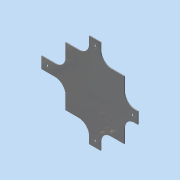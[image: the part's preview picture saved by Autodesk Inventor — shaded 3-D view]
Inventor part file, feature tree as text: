
AUTODESK INVENTOR PART (.ipt)
format: ipt  version: 2015 (Build 190159000, 159)  size: 314,880 bytes
history: native  units: in
note: dims shown in document units (in); Inventor stores cm internally (conversion verified against a paired STEP export)
features: sketch x21, projected_geometry x16, extrude x11, hole x10, pattern_circular x4, chamfer x2, plane x2
ambient origin geometry x8: Origin, YZ Plane, XZ Plane, XY Plane, X Axis, Y Axis, Z Axis, Center Point
bodies: Solid1 (feature_tree)
feature tree (66):
  extrude  "Extrusion1"  Depth=11.811in
  hole  "Hole1"  [1 undecoded]
  hole  "Hole2"  [1 undecoded]
  hole  "Hole3"  [1 undecoded]
  chamfer  "Chamfer1"  Distance=0.125in Angle=45.0deg
  chamfer  "Chamfer2"  Distance=0.125in Angle=45.0deg
  sketch  "Sketch5"  dims[d9=0.2756in]
  extrude  "Extrusion2"  Depth=5.9055in
  plane  "Work Plane1"
  extrude  "Extrusion3"  Depth=5.9055in
  plane  "Work Plane2"
  extrude  "Extrusion4"  Depth=0.1575in TaperAngle=360.0deg
  extrude  "Extrusion5"  Depth=0.1575in TaperAngle=0.0deg
  hole  "Hole5"  [1 undecoded]
  extrude  "Extrusion6"  Depth=0.1575in TaperAngle=0.0deg
  hole  "Hole6"  [1 undecoded]
  extrude  "Extrusion7"  Depth=0.1575in
  hole  "Hole7"  [1 undecoded]
  extrude  "Extrusion8"  Depth=0.1575in TaperAngle=0.0deg
  extrude  "Extrusion9"  Depth=0.1575in
  extrude  "Extrusion10"  Depth=0.1575in
  extrude  "Extrusion11"  Depth=0.1575in TaperAngle=0.0deg
  hole  "Hole8"  [1 undecoded]
  pattern_circular  "Circular Pattern2"  [2 undecoded]
  hole  "Hole9"  [1 undecoded]
  pattern_circular  "Circular Pattern3"  [2 undecoded]
  hole  "Hole10"  [1 undecoded]
  pattern_circular  "Circular Pattern4"  [2 undecoded]
  hole  "Hole11"  [1 undecoded]
  pattern_circular  "Circular Pattern5"  [2 undecoded]
  sketch  "Sketch1"  dims[d0=11.811in d1=11.811in]
  sketch  "Sketch2"  dims[d2=0.125in d3=0.0in d4=0.2756in]
  sketch  "Sketch3"  dims[d5=0.2756in d6=0.2756in]
  sketch  "Sketch4"  dims[d7=0.2756in d8=0.2756in]
  projected_geometry  "Projected Loop1"
  sketch  "Sketch6"  dims[d10=0.2756in]
  projected_geometry  "Projected Loop2"
  projected_geometry  "Projected Loop3"
  projected_geometry  "Projected Loop4"
  projected_geometry  "Projected Loop5"
  projected_geometry  "Projected Loop6"
  projected_geometry  "Projected Loop7"
  projected_geometry  "Projected Loop8"
  sketch  "Sketch7"  dims[d11=0.2756in]
  projected_geometry  "Projected Loop9"
  sketch  "Sketch8"  dims[d12=0.315in d13=0.75in d14=0.375in d15=0.25in d16=0.5635in d17=1.0in d18=0.8108in]
  projected_geometry  "Projected Loop10"
  sketch  "Sketch9"  dims[d19=8.189in]
  sketch  "Sketch10"  dims[d20=8.189in]
  projected_geometry  "Projected Loop11"
  sketch  "Sketch11"  dims[d21=8.189in]
  sketch  "Sketch12"  dims[d22=1.811in]
  projected_geometry  "Projected Loop12"
  sketch  "Sketch13"  dims[d23=1.811in]
  sketch  "Sketch14"  dims[d24=1.811in]
  projected_geometry  "Projected Loop13"
  sketch  "Sketch15"  dims[d25=8.189in]
  projected_geometry  "Projected Loop14"
  sketch  "Sketch16"  dims[d26=1.811in]
  projected_geometry  "Projected Loop15"
  sketch  "Sketch17"  dims[d27=0.1181in d28=0.75in d29=0.375in d30=0.25in d31=0.5635in d32=1.0in d33=0.8108in]
  projected_geometry  "Projected Loop16"
  sketch  "Sketch18"  dims[d38=0.2756in]
  sketch  "Sketch19"  dims[d41=5.9055in]
  sketch  "Sketch20"  dims[d42=0.315in d43=0.75in d44=0.375in d45=0.25in d46=0.5635in d47=1.0in d48=0.8108in d50=2.9528in d51=0.125in d52=45.0deg d53=2.0866in d54=0.125in d55=45.0deg]
  sketch  "Sketch21"  dims[d56=1.9685in d57=5.9055in d58=5.9055in d59=1.5748in d61=360.0deg d63=1.0in d64=0.0in d75=1.0in d76=0.0in d77=1.0in d78=0.0in d79=1.5748in d80=0.0in d81=0.8661in d82=0.2756in d83=0.315in d84=0.75in d85=0.375in d86=0.25in d87=0.5635in d88=1.0in d89=0.8108in d90=0.5906in d91=0.0in d92=0.2756in d93=0.8661in d94=0.315in d95=0.75in d96=0.375in d97=0.25in d98=0.5635in d99=1.0in d100=0.8108in d101=0.5906in d102=0.0in d103=0.8661in d104=0.2756in d105=0.315in d106=0.75in d107=0.375in d108=0.25in d109=0.5635in d110=1.0in d111=0.8108in d112=0.5906in d113=0.0in d114=0.5906in d115=0.0in d116=0.5906in d117=0.0in d118=0.5906in d119=0.0in d120=0.315in d121=0.8661in d122=0.1181in d123=0.2362in d124=0.1575in d125=0.0787in d126=90.0deg d127=0.315in d128=0.8108in d129=1.5748in d130=360.0deg d132=0.315in d133=0.8661in d134=0.1181in d135=0.2362in d136=0.1575in d137=0.0787in d138=90.0deg d139=0.315in d140=0.8108in d141=1.5748in d142=360.0deg d144=0.315in d145=0.8661in d146=0.1181in d147=0.2362in d148=0.1575in d149=0.0787in d150=90.0deg d151=0.315in d152=0.8108in d153=1.5748in d154=360.0deg d156=0.315in d157=0.1181in d158=0.2362in d159=0.1575in d160=0.0787in d161=90.0deg d162=0.315in d163=0.8108in d164=1.5748in d165=360.0deg]
note: 18 required parameter values undecoded (feature->parameter linkage not recoverable at this tier; creation-order binding heuristic only, values carry confidence <= 0.55)
